# Revit family: PH1201QL
name_source: partatom
category: Generic Models
revit_build: Autodesk Revit Architecture 2012 (Build: 20110309_2315(x64)
units: mm (PartAtom-declared; Revit-internal decimal feet)

## types (1)
- PH1201QL
    * = Lens does not ship with projector
    Dimensions (WxDxH) = 27.5 x 36.8 x 12.7 in. / 700 x 935 / 323 mm.
    Environmental - Humidity = 20-80% non-condensing
    Environmental - Operating Temperature = 50deg - 95degF / 10deg - 50degC
    Environmental - Storage = -14deg - 122deg / -10deg - 50degC
    Fan Noise = 48 dB
    Input Current = 8.2A
    Installation Orientation = Floor/Front, Floor/Rear, Ceiling/Front, Ceiling/Rear
    Keynote = Professsional Installation Projectors
    Manufacturer = NEC Dispaly Solutions
    Model = PH1201QL
    Net Weight = 148.9 lbs. / 67.5 kg.
    Optical - Contrast Ratio (up to) = 2000 : 1 with auto iris
    Optical - Display /Technology = 1.38in DMD
    Optical - Laser Life (up to) = 20,000 hours
    Optical - Lens* F-number, f-number  L2K-10F1 = TBD
    Optical - Lens* F-number, f-number  L2K-43ZM1 = TBD
    Optical - Lens* F-number, f-number L2K-55ZM1 = TBD
    Optical - Lens* F-number, f-number NC-50LS12Z = TBD
    Optical - Lens* F-number, f-number NC-50LS14Z = 40.6 - 57.8mm
    Optical - Lens* F-number, f-number NC-50LS16Z = 45.2 - 64.04mm
    Optical - Lens* F-number, f-number NC-50LS18Z = 50.9 - 85.2mm
    Optical - Lens* F-number, f-number NC-50LS21Z = 60.8 - 102.3mm
    Optical - Lens* Focus = Powered with Lens Memory
    Optical - Lens* Shift = Powered +0.5 / -0 vertical, +0.06 / -0.08 horizontal
    Optical - Lens* Zoom = Powered with Lens Memory
    Optical - Lens* Zoom Ratio = Lens Dependent
    Optical - Projection Angle = Variable
    Optical - Projection Distance = Variable
    Optical - Resolution Maximum = QXGA 4096 x 2160
    Optical - Resolution Native = DC4K 4096 x 2160
    Optical - Screen Size (diagonal) = 80 to 500in. / 2.03 to 12.7m.
    Optical - Throw Ratio L2K-10F1 = 0.9 : 1
    Optical - Throw Ratio L2K-43ZM1 = 3.70 - 5.30 : 1
    Optical - Throw Ratio L2K-55ZM1 = 4.80 - 7.40 : 1
    Optical - Throw Ratio NC-50LS12Z = 1.13 - 1.66 : 1
    Optical - Throw Ratio NC-50LS14Z = 1.30 - 1.85 : 1
    Optical - Throw Ratio NC-50LS16Z = 1.45 - 2.17 : 1
    Optical - Throw Ratio NC-50LS18Z = 1.63 - 2.71 : 1
    Optical - Throw Ratio NC-50LS21Z = 1.95 - 3.26 : 1
    Power Consumption (ECO off/ECO Mode/Standby/Standby-Power Saving) = 1608W
    Power Requirements = 200 - 240V AC, 50/60Hz
    Regulations = USA: UL 1950 FCC Class B, Canada: CSA950 (C-UL), NOM
    Signal Compatibility/Connectivity - External Control = RS-232, Wired, Remote, USB (Service Port0)
    Signal Compatibility/Connectivity - Input/Output Terminals RGB1 (analog) = HDMI w/ HDCP
    Signal Compatibility/Connectivity - Input/Output Terminals RGB2 (analog) = HDMI w/ HDCP
    Signal Compatibility/Connectivity - Input/Output Terminals RGB3 (analog) = DisplayPort w/ HDCP
    Signal Compatibility/Connectivity - Input/Output Terminals RGB4 (digital) = DisplayPort w/ HDCP
    Signal Compatibility/Connectivity - Macintosh Compatibility = Yes
    Signal Compatibility/Connectivity - SD/HD Video Signal Compatibility = 480i, 480p, 576i, 576p, 720p, 1080i, 1080p
    Signal Compatibility/Connectivity - Scan Rate, Horizontal = 15 - 108 kHz
    Signal Compatibility/Connectivity - Scan Rate, Vertical = 48 - 120 Hz
    Signal Compatibility/Connectivity - Supported Video Standards = NTSC, NTSC4.43, PAL, PAL-60, PAL-M, PAL-N, SECAM
    Signal Compatibility/Connectivity - Sync Compatibility = Separate Sync /Composite Sync / Sync on G
    URL = www.necdisplay.com

## geometry (parser evidence)
native form markers: Sweep x2
no freeform markers — native parametric forms only
